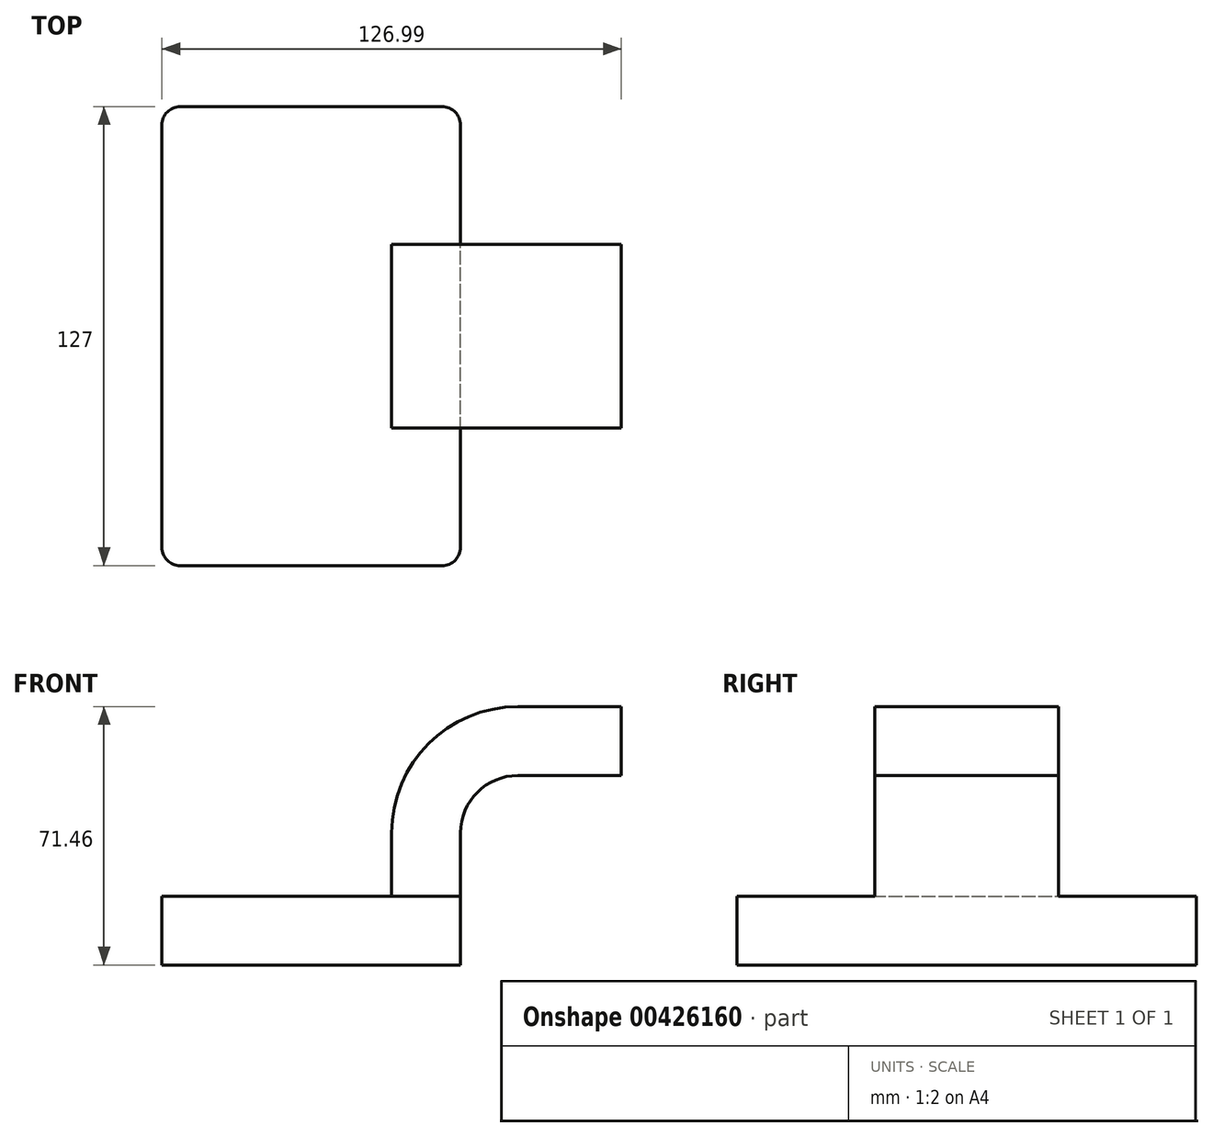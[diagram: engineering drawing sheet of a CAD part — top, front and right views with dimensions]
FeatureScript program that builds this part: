
annotation { "Feature Type Name" : "Feature", "Feature Type Description" : "" }
export const myFeature = defineFeature(function(context is Context, id is Id, definition is map)
    precondition{}
    {
        {
            var Q0;
            Q0=qCreatedBy(makeId("Front.planeOp"),FACE);
            var sketch = newSketch(context, id + "F0", { "sketchPlane" : qUnion([Q0])});
            skLineSegment(sketch, "E0.bottom", {"start": v(41.28, -9.52) * mm, "end": v(-41.28, -9.53) * mm});
            skLineSegment(sketch, "E0.top", {"start": v(41.28, 9.53) * mm, "end": v(-41.28, 9.53) * mm});
            skLineSegment(sketch, "E0.left", {"start": v(41.28, -9.52) * mm, "end": v(41.28, 9.53) * mm});
            skLineSegment(sketch, "E0.right", {"start": v(-41.28, -9.53) * mm, "end": v(-41.28, 9.53) * mm});
            skPoint(sketch, "E0.middle", {"position": v(0, 0) * mm});
            skLineSegment(sketch, "E1.bottom", {"start": v(60.32, 66.68) * mm, "end": v(111.12, 66.68) * mm});
            skLineSegment(sketch, "E1.top", {"start": v(60.32, 38.1) * mm, "end": v(111.12, 38.1) * mm});
            skLineSegment(sketch, "E1.left", {"start": v(60.32, 66.68) * mm, "end": v(60.32, 38.1) * mm});
            skLineSegment(sketch, "E1.right", {"start": v(111.12, 66.68) * mm, "end": v(111.12, 38.1) * mm});
            skPoint(sketch, "E1.middle", {"position": v(85.72, 52.39) * mm});
            skLineSegment(sketch, "E2", {"start": v(41.28, 9.53) * mm, "end": v(41.28, 27) * mm});
            skArc(sketch, "E3", {"start": v(41.27, 27) * mm, "mid": v(45.92, 38.23) * mm, "end": v(57.15, 42.88) * mm});
            skLineSegment(sketch, "E4", {"start": v(57.15, 42.88) * mm, "end": v(85.72, 42.88) * mm});
            skLineSegment(sketch, "E5.0", {"start": v(57.15, 61.93) * mm, "end": v(85.72, 61.93) * mm});
            skArc(sketch, "E5.1", {"start": v(22.23, 27) * mm, "mid": v(32.45, 51.7) * mm, "end": v(57.15, 61.93) * mm});
            skLineSegment(sketch, "E5.2", {"start": v(22.22, 9.53) * mm, "end": v(22.22, 27) * mm});
            skLineSegment(sketch, "E6", {"start": v(85.72, 38.1) * mm, "end": v(85.72, 66.68) * mm});
            skFitSpline(sketch, "E7", {"points": [v(-41.28, 9.53) * mm, v(57.15, 61.93) * mm], "startDerivative": vector(22.51, 68.2) * mm, "endDerivative": vector(171.45, -12.22) * mm});
            skSolve(sketch);
        }
        {
            var Q0;
            Q0=makeQuery(id+"F0.imprint","IMPRINT",FACE,{"disambiguationData":[TD([[makeQuery(id+"F0.imprint","IMPRINT",EDGE,{"derivedFrom":sQuery(id+"F0.wireOp",EDGE,"E0.bottom")}),-1.0]])]});
            extrude(context, id + "F1", {"entities" : qUnion([Q0]), "endBound" : BoundingType.SYMMETRIC, "depth" : 127 * mm});
        }
        {
            var Q0;
            {var subQ1=sQuery(id+"F0.wireOp",EDGE,"E2");Q0=makeQuery(id+"F0.imprint","IMPRINT",FACE,{"disambiguationData":[TD([[makeQuery(id+"F0.imprint","IMPRINT",EDGE,{"derivedFrom":subQ1}),1.0]])]});}
            var Q1;
            {var subQ0=sQuery(id+"F0.wireOp",EDGE,"E5.0");var subQ1=sQuery(id+"F0.wireOp",EDGE,"E1.left");var subQ2=makeQuery(id+"F0.imprint","INTERSECT",VERTEX,{"derivedFrom":[subQ1,subQ0]});Q1=makeQuery(id+"F0.imprint","IMPRINT",FACE,{"disambiguationData":[TD([[makeQuery(id+"F0.imprint","IMPRINT",EDGE,{"disambiguationData":[TD([[subQ2,-1.0]])],"derivedFrom":subQ1}),1.0]])]});}
            extrude(context, id + "F2", {"entities" : qUnion([Q0, Q1]), "operationType" : NewBodyOperationType.ADD, "endBound" : BoundingType.SYMMETRIC, "depth" : 50.8 * mm});
        }
        {
            var Q0;
            Q0=makeQuery(id+"F0.imprint","IMPRINT",FACE,{"disambiguationData":[TD([[makeQuery(id+"F0.imprint","IMPRINT",EDGE,{"derivedFrom":sQuery(id+"F0.wireOp",EDGE,"E5.1")}),1.0]])]});
            extrude(context, id + "F3", {"entities" : qUnion([Q0]), "operationType" : NewBodyOperationType.ADD, "endBound" : BoundingType.SYMMETRIC, "depth" : 15.88 * mm});
        }
        {
            var Q0;
            Q0=makeQuery(id+"F1.opExtrude","CAP_EDGE",EDGE,{"disambiguationData":[OSD([sQuery(id+"F0.wireOp",EDGE,"E0.left")])],"isStart":false});
            var Q1;
            Q1=makeQuery(id+"F1.opExtrude","CAP_EDGE",EDGE,{"disambiguationData":[OSD([sQuery(id+"F0.wireOp",EDGE,"E0.left")])],"isStart":true});
            var Q2;
            Q2=makeQuery(id+"F1.opExtrude","CAP_EDGE",EDGE,{"disambiguationData":[OSD([sQuery(id+"F0.wireOp",EDGE,"E0.right")])],"isStart":true});
            var Q3;
            Q3=makeQuery(id+"F1.opExtrude","CAP_EDGE",EDGE,{"disambiguationData":[OSD([sQuery(id+"F0.wireOp",EDGE,"E0.right")])],"isStart":false});
            fillet(context, id + "F4", {"entities" : qUnion([Q0, Q1, Q2, Q3]), "radius" : 5.08 * mm, "tangentPropagation" : true, "allowEdgeOverflow" : false});
        }
    });
